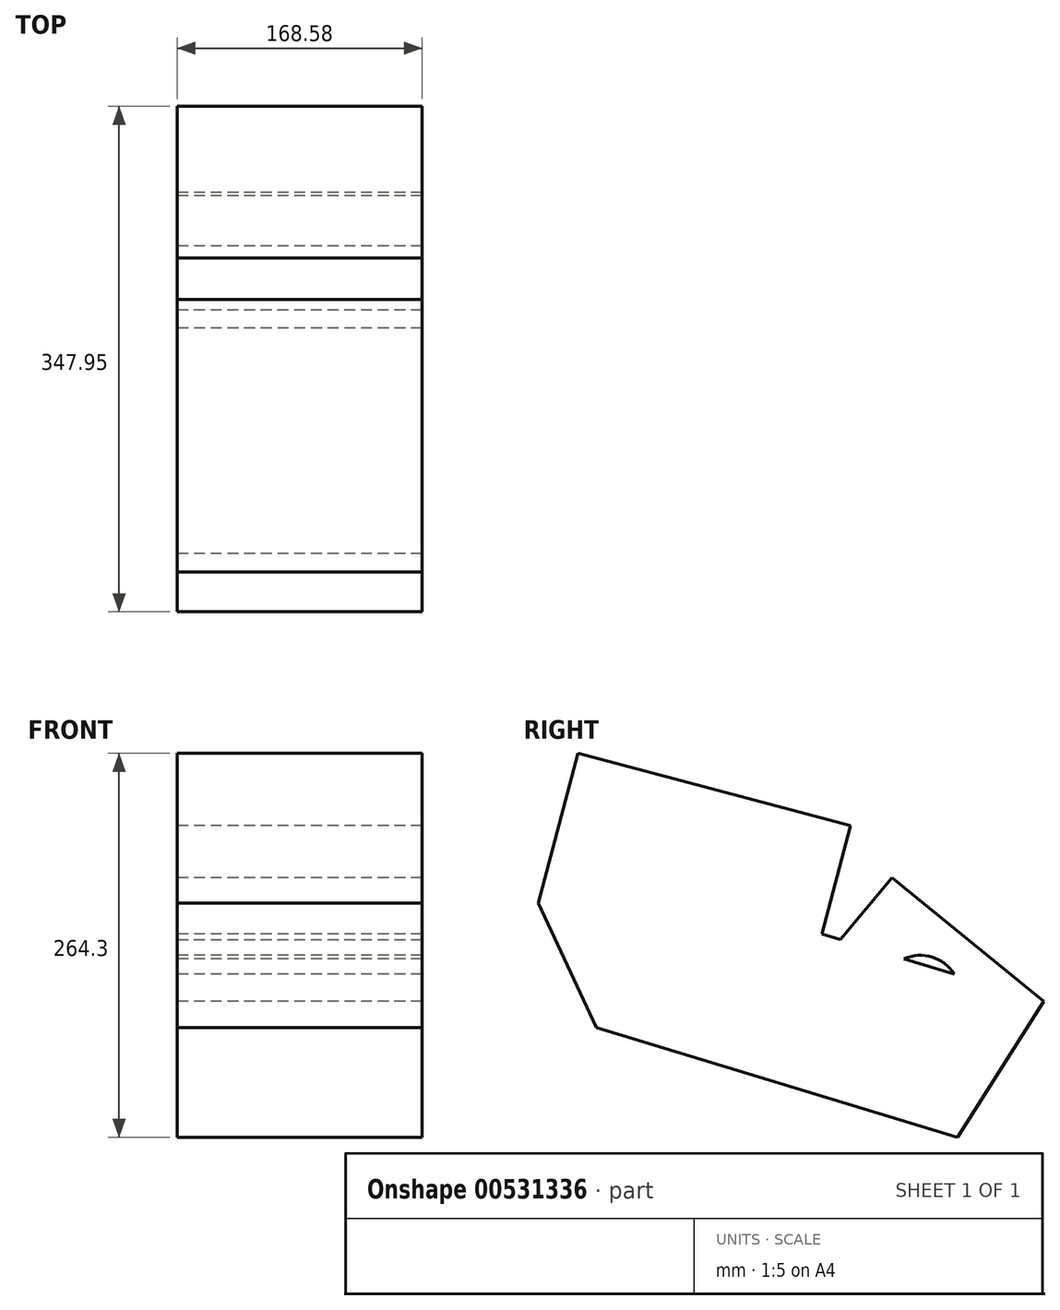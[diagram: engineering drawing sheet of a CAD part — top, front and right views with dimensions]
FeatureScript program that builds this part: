
annotation { "Feature Type Name" : "Feature", "Feature Type Description" : "" }
export const myFeature = defineFeature(function(context is Context, id is Id, definition is map)
    precondition{}
    {
        {
            var Q0;
            Q0=qCreatedBy(makeId("Right.planeOp"),FACE);
            var sketch = newSketch(context, id + "F0", { "sketchPlane" : qUnion([Q0])});
            skLineSegment(sketch, "E0", {"start": v(-13.14, 13.4) * mm, "end": v(-200.8, 63.1) * mm});
            skLineSegment(sketch, "E1", {"start": v(-200.8, 63.1) * mm, "end": v(-160.74, -22.59) * mm});
            skLineSegment(sketch, "E2", {"start": v(-160.74, -22.59) * mm, "end": v(87.77, -97.95) * mm});
            skLineSegment(sketch, "E3", {"start": v(87.77, -97.95) * mm, "end": v(147.14, -4.53) * mm});
            skLineSegment(sketch, "E4", {"start": v(147.14, -4.53) * mm, "end": v(42.59, 80.67) * mm});
            skLineSegment(sketch, "E5", {"start": v(42.59, 80.67) * mm, "end": v(-13.14, 13.4) * mm});
            skCircle(sketch, "E6", {"center": v(62.33, 0) * mm, "radius": 27.24 * mm});
            skSolve(sketch);
        }
        {
            var Q0;
            Q0 = qSketchRegion(id + "F0", true);
            extrude(context, id + "F1", {"entities" : qUnion([Q0]), "depth" : 168.58 * mm, "offsetDistance" : 25.4 * mm});
        }
        {
            var Q0;
            Q0=makeQuery(id+"F1.opExtrude","SWEPT_FACE",FACE,{"disambiguationData":[OSD([sQuery(id+"F0.wireOp",EDGE,"E0")])]});
            var Q1;
            Q1=makeQuery(id+"F1.opExtrude","SWEPT_FACE",FACE,{"disambiguationData":[OSD([sQuery(id+"F0.wireOp",EDGE,"E2")])]});
            extrude(context, id + "F2", {"entities" : qUnion([Q0, Q1]), "operationType" : NewBodyOperationType.ADD, "depth" : 106.8 * mm, "offsetDistance" : 25.4 * mm});
        }
    });
